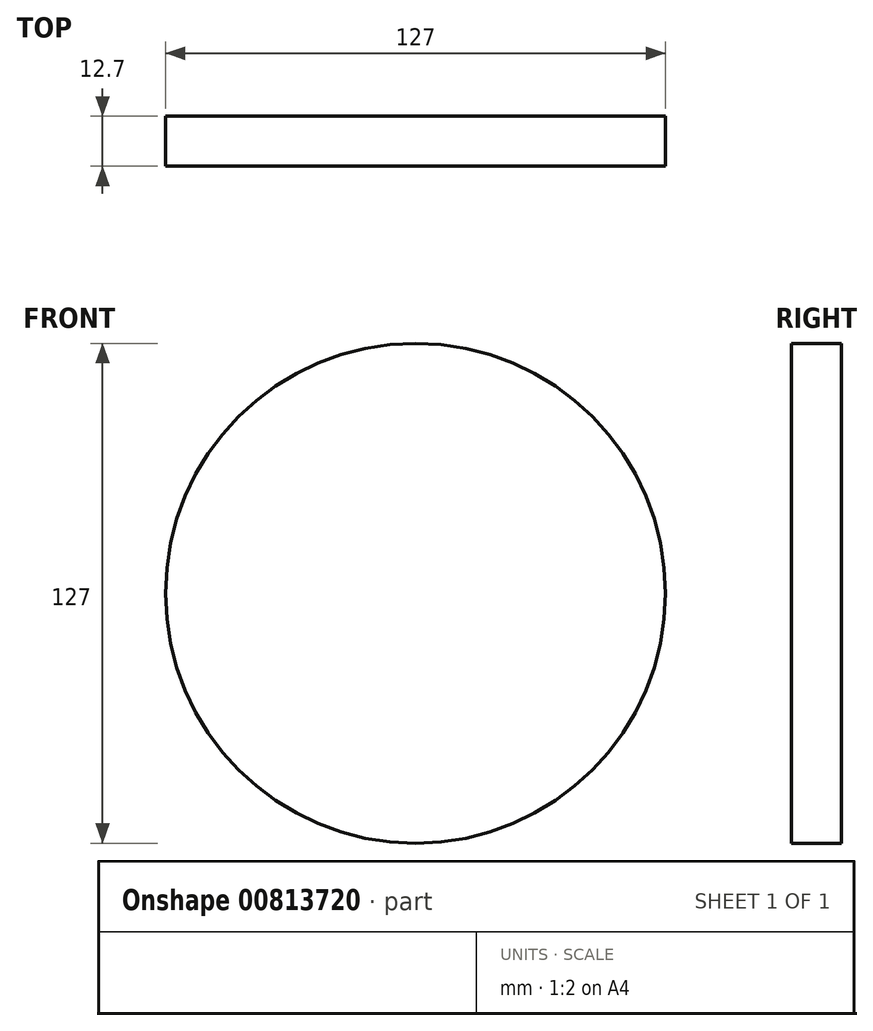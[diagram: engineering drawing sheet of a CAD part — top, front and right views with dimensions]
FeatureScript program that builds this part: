
annotation { "Feature Type Name" : "Feature", "Feature Type Description" : "" }
export const myFeature = defineFeature(function(context is Context, id is Id, definition is map)
    precondition{}
    {
        {
            var Q0;
            Q0=qCreatedBy(makeId("Front.planeOp"),FACE);
            var sketch = newSketch(context, id + "F0", { "sketchPlane" : qUnion([Q0])});
            skCircle(sketch, "E0", {"center": v(0, 0) * mm, "radius": 63.5 * mm});
            skSolve(sketch);
        }
        {
            var Q0;
            Q0 = qSketchRegion(id + "F0", true);
            extrude(context, id + "F1", {"entities" : qUnion([Q0]), "depth" : 12.7 * mm, "offsetDistance" : 25.4 * mm});
        }
    });
